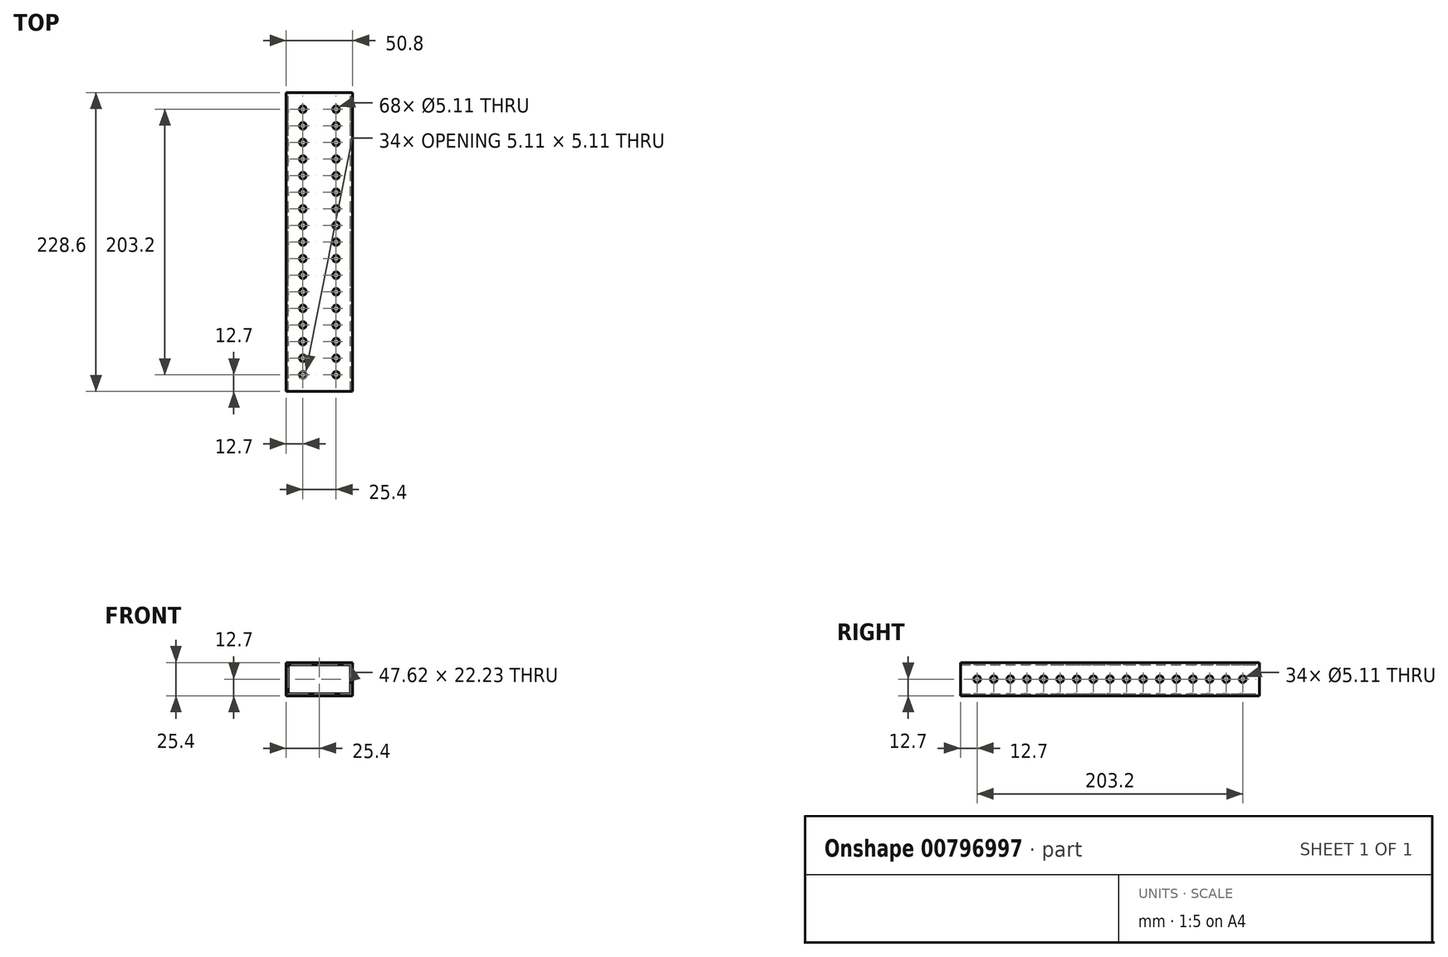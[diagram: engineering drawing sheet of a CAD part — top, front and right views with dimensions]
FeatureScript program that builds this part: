
annotation { "Feature Type Name" : "Feature", "Feature Type Description" : "" }
export const myFeature = defineFeature(function(context is Context, id is Id, definition is map)
    precondition{}
    {
        {
            var Q0;
            Q0=qCreatedBy(makeId("Front.planeOp"),FACE);
            var sketch = newSketch(context, id + "F0", { "sketchPlane" : qUnion([Q0])});
            skLineSegment(sketch, "E0.bottom", {"start": v(-25.4, 12.7) * mm, "end": v(25.4, 12.7) * mm});
            skLineSegment(sketch, "E0.top", {"start": v(-25.4, -12.7) * mm, "end": v(25.4, -12.7) * mm});
            skLineSegment(sketch, "E0.left", {"start": v(-25.4, 12.7) * mm, "end": v(-25.4, -12.7) * mm});
            skLineSegment(sketch, "E0.right", {"start": v(25.4, 12.7) * mm, "end": v(25.4, -12.7) * mm});
            skPoint(sketch, "E0.middle", {"position": v(0, 0) * mm});
            skLineSegment(sketch, "E1.0", {"start": v(-23.81, -11.11) * mm, "end": v(23.81, -11.11) * mm});
            skLineSegment(sketch, "E1.1", {"start": v(-23.81, 11.11) * mm, "end": v(-23.81, -11.11) * mm});
            skLineSegment(sketch, "E1.2", {"start": v(-23.81, 11.11) * mm, "end": v(23.81, 11.11) * mm});
            skLineSegment(sketch, "E1.3", {"start": v(23.81, 11.11) * mm, "end": v(23.81, -11.11) * mm});
            skSolve(sketch);
        }
        {
            var Q0;
            Q0 = qSketchRegion(id + "F0", true);
            extrude(context, id + "F1", {"entities" : qUnion([Q0]), "depth" : 228.6 * mm, "offsetDistance" : 25.4 * mm});
        }
        {
            var Q0;
            Q0=makeQuery(id+"F1.opExtrude","SWEPT_FACE",FACE,{"disambiguationData":[OSD([sQuery(id+"F0.wireOp",EDGE,"E0.left")])]});
            var sketch = newSketch(context, id + "F2", { "sketchPlane" : qUnion([Q0])});
            skCircle(sketch, "E2", {"center": v(12.7, 0) * mm, "radius": 2.55 * mm});
            skCircle(sketch, "E3.1.0.0", {"center": v(25.4, 0) * mm, "radius": 2.55 * mm});
            skCircle(sketch, "E3.2.0.0", {"center": v(38.1, 0) * mm, "radius": 2.55 * mm});
            skCircle(sketch, "E3.3.0.0", {"center": v(50.8, 0) * mm, "radius": 2.55 * mm});
            skCircle(sketch, "E3.4.0.0", {"center": v(63.5, 0) * mm, "radius": 2.55 * mm});
            skCircle(sketch, "E3.5.0.0", {"center": v(76.2, 0) * mm, "radius": 2.55 * mm});
            skCircle(sketch, "E3.6.0.0", {"center": v(88.9, 0) * mm, "radius": 2.55 * mm});
            skCircle(sketch, "E3.7.0.0", {"center": v(101.6, 0) * mm, "radius": 2.55 * mm});
            skCircle(sketch, "E3.8.0.0", {"center": v(114.3, 0) * mm, "radius": 2.55 * mm});
            skCircle(sketch, "E3.9.0.0", {"center": v(127, 0) * mm, "radius": 2.55 * mm});
            skCircle(sketch, "E3.10.0.0", {"center": v(139.7, 0) * mm, "radius": 2.55 * mm});
            skCircle(sketch, "E3.11.0.0", {"center": v(152.4, 0) * mm, "radius": 2.55 * mm});
            skCircle(sketch, "E3.12.0.0", {"center": v(165.1, 0) * mm, "radius": 2.55 * mm});
            skCircle(sketch, "E3.13.0.0", {"center": v(177.8, 0) * mm, "radius": 2.55 * mm});
            skCircle(sketch, "E3.14.0.0", {"center": v(190.5, 0) * mm, "radius": 2.55 * mm});
            skCircle(sketch, "E3.15.0.0", {"center": v(203.2, 0) * mm, "radius": 2.55 * mm});
            skCircle(sketch, "E3.16.0.0", {"center": v(215.9, 0) * mm, "radius": 2.55 * mm});
            skLineSegment(sketch, "E3.direction1", {"start": v(12.7, 0) * mm, "end": v(25.4, 0) * mm, "construction": true});
            skSolve(sketch);
        }
        {
            var Q0;
            Q0=makeQuery(id+"F2.imprint","IMPRINT",FACE,{"disambiguationData":[TD([[makeQuery(id+"F2.imprint","IMPRINT",EDGE,{"derivedFrom":sQuery(id+"F2.wireOp",EDGE,"E2")}),1.0]])]});
            var Q1;
            Q1=makeQuery(id+"F2.imprint","IMPRINT",FACE,{"disambiguationData":[TD([[makeQuery(id+"F2.imprint","IMPRINT",EDGE,{"derivedFrom":sQuery(id+"F2.wireOp",EDGE,"E3.1.0.0")}),1.0]])]});
            var Q2;
            Q2=makeQuery(id+"F2.imprint","IMPRINT",FACE,{"disambiguationData":[TD([[makeQuery(id+"F2.imprint","IMPRINT",EDGE,{"derivedFrom":sQuery(id+"F2.wireOp",EDGE,"E3.2.0.0")}),1.0]])]});
            var Q3;
            Q3=makeQuery(id+"F2.imprint","IMPRINT",FACE,{"disambiguationData":[TD([[makeQuery(id+"F2.imprint","IMPRINT",EDGE,{"derivedFrom":sQuery(id+"F2.wireOp",EDGE,"E3.3.0.0")}),1.0]])]});
            var Q4;
            Q4=makeQuery(id+"F2.imprint","IMPRINT",FACE,{"disambiguationData":[TD([[makeQuery(id+"F2.imprint","IMPRINT",EDGE,{"derivedFrom":sQuery(id+"F2.wireOp",EDGE,"E3.4.0.0")}),1.0]])]});
            var Q5;
            Q5=makeQuery(id+"F2.imprint","IMPRINT",FACE,{"disambiguationData":[TD([[makeQuery(id+"F2.imprint","IMPRINT",EDGE,{"derivedFrom":sQuery(id+"F2.wireOp",EDGE,"E3.6.0.0")}),1.0]])]});
            var Q6;
            Q6=makeQuery(id+"F2.imprint","IMPRINT",FACE,{"disambiguationData":[TD([[makeQuery(id+"F2.imprint","IMPRINT",EDGE,{"derivedFrom":sQuery(id+"F2.wireOp",EDGE,"E3.7.0.0")}),1.0]])]});
            var Q7;
            Q7=makeQuery(id+"F2.imprint","IMPRINT",FACE,{"disambiguationData":[TD([[makeQuery(id+"F2.imprint","IMPRINT",EDGE,{"derivedFrom":sQuery(id+"F2.wireOp",EDGE,"E3.5.0.0")}),1.0]])]});
            var Q8;
            Q8=makeQuery(id+"F2.imprint","IMPRINT",FACE,{"disambiguationData":[TD([[makeQuery(id+"F2.imprint","IMPRINT",EDGE,{"derivedFrom":sQuery(id+"F2.wireOp",EDGE,"E3.8.0.0")}),1.0]])]});
            var Q9;
            Q9=makeQuery(id+"F2.imprint","IMPRINT",FACE,{"disambiguationData":[TD([[makeQuery(id+"F2.imprint","IMPRINT",EDGE,{"derivedFrom":sQuery(id+"F2.wireOp",EDGE,"E3.9.0.0")}),1.0]])]});
            var Q10;
            Q10=makeQuery(id+"F2.imprint","IMPRINT",FACE,{"disambiguationData":[TD([[makeQuery(id+"F2.imprint","IMPRINT",EDGE,{"derivedFrom":sQuery(id+"F2.wireOp",EDGE,"E3.10.0.0")}),1.0]])]});
            var Q11;
            Q11=makeQuery(id+"F2.imprint","IMPRINT",FACE,{"disambiguationData":[TD([[makeQuery(id+"F2.imprint","IMPRINT",EDGE,{"derivedFrom":sQuery(id+"F2.wireOp",EDGE,"E3.11.0.0")}),1.0]])]});
            var Q12;
            Q12=makeQuery(id+"F2.imprint","IMPRINT",FACE,{"disambiguationData":[TD([[makeQuery(id+"F2.imprint","IMPRINT",EDGE,{"derivedFrom":sQuery(id+"F2.wireOp",EDGE,"E3.12.0.0")}),1.0]])]});
            var Q13;
            Q13=makeQuery(id+"F2.imprint","IMPRINT",FACE,{"disambiguationData":[TD([[makeQuery(id+"F2.imprint","IMPRINT",EDGE,{"derivedFrom":sQuery(id+"F2.wireOp",EDGE,"E3.13.0.0")}),1.0]])]});
            var Q14;
            Q14=makeQuery(id+"F2.imprint","IMPRINT",FACE,{"disambiguationData":[TD([[makeQuery(id+"F2.imprint","IMPRINT",EDGE,{"derivedFrom":sQuery(id+"F2.wireOp",EDGE,"E3.14.0.0")}),1.0]])]});
            var Q15;
            Q15=makeQuery(id+"F2.imprint","IMPRINT",FACE,{"disambiguationData":[TD([[makeQuery(id+"F2.imprint","IMPRINT",EDGE,{"derivedFrom":sQuery(id+"F2.wireOp",EDGE,"E3.15.0.0")}),1.0]])]});
            var Q16;
            Q16=makeQuery(id+"F2.imprint","IMPRINT",FACE,{"disambiguationData":[TD([[makeQuery(id+"F2.imprint","IMPRINT",EDGE,{"derivedFrom":sQuery(id+"F2.wireOp",EDGE,"E3.16.0.0")}),1.0]])]});
            var Q17;
            Q17=makeQuery(id+"F2.imprint","IMPRINT",FACE,{"disambiguationData":[TD([[makeQuery(id+"F2.imprint","IMPRINT",EDGE,{"derivedFrom":sQuery(id+"F2.wireOp",EDGE,"E3.17.0.0")}),1.0]])]});
            var Q18;
            Q18=makeQuery(id+"F2.imprint","IMPRINT",FACE,{"disambiguationData":[TD([[makeQuery(id+"F2.imprint","IMPRINT",EDGE,{"derivedFrom":sQuery(id+"F2.wireOp",EDGE,"E3.18.0.0")}),1.0]])]});
            extrude(context, id + "F3", {"entities" : qUnion([Q0, Q1, Q2, Q3, Q4, Q5, Q6, Q7, Q8, Q9, Q10, Q11, Q12, Q13, Q14, Q15, Q16, Q17, Q18]), "operationType" : NewBodyOperationType.REMOVE, "oppositeDirection" : true, "depth" : 279.4 * mm, "offsetDistance" : 25.4 * mm});
        }
        {
            var Q0;
            Q0=makeQuery(id+"F1.opExtrude","SWEPT_FACE",FACE,{"disambiguationData":[OSD([sQuery(id+"F0.wireOp",EDGE,"E0.top")])]});
            var sketch = newSketch(context, id + "F4", { "sketchPlane" : qUnion([Q0])});
            skCircle(sketch, "E4", {"center": v(-12.7, 215.9) * mm, "radius": 2.55 * mm});
            skCircle(sketch, "E5.0.1.0", {"center": v(-12.7, 203.2) * mm, "radius": 2.55 * mm});
            skCircle(sketch, "E5.0.2.0", {"center": v(-12.7, 190.5) * mm, "radius": 2.55 * mm});
            skCircle(sketch, "E5.0.3.0", {"center": v(-12.7, 177.8) * mm, "radius": 2.55 * mm});
            skCircle(sketch, "E5.0.4.0", {"center": v(-12.7, 165.1) * mm, "radius": 2.55 * mm});
            skCircle(sketch, "E5.0.5.0", {"center": v(-12.7, 152.4) * mm, "radius": 2.55 * mm});
            skCircle(sketch, "E5.0.6.0", {"center": v(-12.7, 139.7) * mm, "radius": 2.55 * mm});
            skCircle(sketch, "E5.0.7.0", {"center": v(-12.7, 127) * mm, "radius": 2.55 * mm});
            skCircle(sketch, "E5.0.8.0", {"center": v(-12.7, 114.3) * mm, "radius": 2.55 * mm});
            skCircle(sketch, "E5.0.9.0", {"center": v(-12.7, 101.6) * mm, "radius": 2.55 * mm});
            skCircle(sketch, "E5.0.10.0", {"center": v(-12.7, 88.9) * mm, "radius": 2.55 * mm});
            skCircle(sketch, "E5.0.11.0", {"center": v(-12.7, 76.2) * mm, "radius": 2.55 * mm});
            skCircle(sketch, "E5.0.12.0", {"center": v(-12.7, 63.5) * mm, "radius": 2.55 * mm});
            skCircle(sketch, "E5.0.13.0", {"center": v(-12.7, 50.8) * mm, "radius": 2.55 * mm});
            skCircle(sketch, "E5.0.14.0", {"center": v(-12.7, 38.1) * mm, "radius": 2.55 * mm});
            skCircle(sketch, "E5.0.15.0", {"center": v(-12.7, 25.4) * mm, "radius": 2.55 * mm});
            skCircle(sketch, "E5.0.16.0", {"center": v(-12.7, 12.7) * mm, "radius": 2.55 * mm});
            skCircle(sketch, "E5.1.0.0", {"center": v(12.7, 215.9) * mm, "radius": 2.55 * mm});
            skCircle(sketch, "E5.1.1.0", {"center": v(12.7, 203.2) * mm, "radius": 2.55 * mm});
            skCircle(sketch, "E5.1.2.0", {"center": v(12.7, 190.5) * mm, "radius": 2.55 * mm});
            skCircle(sketch, "E5.1.3.0", {"center": v(12.7, 177.8) * mm, "radius": 2.55 * mm});
            skCircle(sketch, "E5.1.4.0", {"center": v(12.7, 165.1) * mm, "radius": 2.55 * mm});
            skCircle(sketch, "E5.1.5.0", {"center": v(12.7, 152.4) * mm, "radius": 2.55 * mm});
            skCircle(sketch, "E5.1.6.0", {"center": v(12.7, 139.7) * mm, "radius": 2.55 * mm});
            skCircle(sketch, "E5.1.7.0", {"center": v(12.7, 127) * mm, "radius": 2.55 * mm});
            skCircle(sketch, "E5.1.8.0", {"center": v(12.7, 114.3) * mm, "radius": 2.55 * mm});
            skCircle(sketch, "E5.1.9.0", {"center": v(12.7, 101.6) * mm, "radius": 2.55 * mm});
            skCircle(sketch, "E5.1.10.0", {"center": v(12.7, 88.9) * mm, "radius": 2.55 * mm});
            skCircle(sketch, "E5.1.11.0", {"center": v(12.7, 76.2) * mm, "radius": 2.55 * mm});
            skCircle(sketch, "E5.1.12.0", {"center": v(12.7, 63.5) * mm, "radius": 2.55 * mm});
            skCircle(sketch, "E5.1.13.0", {"center": v(12.7, 50.8) * mm, "radius": 2.55 * mm});
            skCircle(sketch, "E5.1.14.0", {"center": v(12.7, 38.1) * mm, "radius": 2.55 * mm});
            skCircle(sketch, "E5.1.15.0", {"center": v(12.7, 25.4) * mm, "radius": 2.55 * mm});
            skCircle(sketch, "E5.1.16.0", {"center": v(12.7, 12.7) * mm, "radius": 2.55 * mm});
            skLineSegment(sketch, "E5.direction1", {"start": v(-12.7, 215.9) * mm, "end": v(12.7, 215.9) * mm, "construction": true});
            skLineSegment(sketch, "E5.direction2", {"start": v(-12.7, 215.9) * mm, "end": v(-12.7, 203.2) * mm, "construction": true});
            skLineSegment(sketch, "E6.bottom", {"start": v(-25.4, 228.6) * mm, "end": v(25.4, 228.6) * mm});
            skLineSegment(sketch, "E6.top", {"start": v(-25.4, 0) * mm, "end": v(25.4, 0) * mm});
            skLineSegment(sketch, "E6.left", {"start": v(-25.4, 228.6) * mm, "end": v(-25.4, 0) * mm});
            skLineSegment(sketch, "E6.right", {"start": v(25.4, 228.6) * mm, "end": v(25.4, 0) * mm});
            skSolve(sketch);
        }
        {
            var Q0;
            Q0=makeQuery(id+"F4.imprint","IMPRINT",FACE,{"disambiguationData":[TD([[makeQuery(id+"F4.imprint","IMPRINT",EDGE,{"derivedFrom":sQuery(id+"F4.wireOp",EDGE,"E5.1.15.0")}),1.0]])]});
            var Q1;
            Q1=makeQuery(id+"F4.imprint","IMPRINT",FACE,{"disambiguationData":[TD([[makeQuery(id+"F4.imprint","IMPRINT",EDGE,{"derivedFrom":sQuery(id+"F4.wireOp",EDGE,"E5.0.15.0")}),1.0]])]});
            var Q2;
            Q2=makeQuery(id+"F4.imprint","IMPRINT",FACE,{"disambiguationData":[TD([[makeQuery(id+"F4.imprint","IMPRINT",EDGE,{"derivedFrom":sQuery(id+"F4.wireOp",EDGE,"E5.0.7.0")}),1.0]])]});
            var Q3;
            Q3=makeQuery(id+"F4.imprint","IMPRINT",FACE,{"disambiguationData":[TD([[makeQuery(id+"F4.imprint","IMPRINT",EDGE,{"derivedFrom":sQuery(id+"F4.wireOp",EDGE,"E5.0.9.0")}),1.0]])]});
            var Q4;
            Q4=makeQuery(id+"F4.imprint","IMPRINT",FACE,{"disambiguationData":[TD([[makeQuery(id+"F4.imprint","IMPRINT",EDGE,{"derivedFrom":sQuery(id+"F4.wireOp",EDGE,"E5.1.17.0")}),1.0]])]});
            var Q5;
            Q5=makeQuery(id+"F4.imprint","IMPRINT",FACE,{"disambiguationData":[TD([[makeQuery(id+"F4.imprint","IMPRINT",EDGE,{"derivedFrom":sQuery(id+"F4.wireOp",EDGE,"E5.1.18.0")}),1.0]])]});
            var Q6;
            Q6=makeQuery(id+"F4.imprint","IMPRINT",FACE,{"disambiguationData":[TD([[makeQuery(id+"F4.imprint","IMPRINT",EDGE,{"derivedFrom":sQuery(id+"F4.wireOp",EDGE,"E5.1.5.0")}),1.0]])]});
            var Q7;
            Q7=makeQuery(id+"F4.imprint","IMPRINT",FACE,{"disambiguationData":[TD([[makeQuery(id+"F4.imprint","IMPRINT",EDGE,{"derivedFrom":sQuery(id+"F4.wireOp",EDGE,"E5.0.3.0")}),1.0]])]});
            var Q8;
            Q8=makeQuery(id+"F4.imprint","IMPRINT",FACE,{"disambiguationData":[TD([[makeQuery(id+"F4.imprint","IMPRINT",EDGE,{"derivedFrom":sQuery(id+"F4.wireOp",EDGE,"E5.1.12.0")}),1.0]])]});
            var Q9;
            Q9=makeQuery(id+"F4.imprint","IMPRINT",FACE,{"disambiguationData":[TD([[makeQuery(id+"F4.imprint","IMPRINT",EDGE,{"derivedFrom":sQuery(id+"F4.wireOp",EDGE,"E5.1.2.0")}),1.0]])]});
            var Q10;
            Q10=makeQuery(id+"F4.imprint","IMPRINT",FACE,{"disambiguationData":[TD([[makeQuery(id+"F4.imprint","IMPRINT",EDGE,{"derivedFrom":sQuery(id+"F4.wireOp",EDGE,"E5.1.9.0")}),1.0]])]});
            var Q11;
            Q11=makeQuery(id+"F4.imprint","IMPRINT",FACE,{"disambiguationData":[TD([[makeQuery(id+"F4.imprint","IMPRINT",EDGE,{"derivedFrom":sQuery(id+"F4.wireOp",EDGE,"E5.0.11.0")}),1.0]])]});
            var Q12;
            Q12=makeQuery(id+"F4.imprint","IMPRINT",FACE,{"disambiguationData":[TD([[makeQuery(id+"F4.imprint","IMPRINT",EDGE,{"derivedFrom":sQuery(id+"F4.wireOp",EDGE,"E5.0.6.0")}),1.0]])]});
            var Q13;
            Q13=makeQuery(id+"F4.imprint","IMPRINT",FACE,{"disambiguationData":[TD([[makeQuery(id+"F4.imprint","IMPRINT",EDGE,{"derivedFrom":sQuery(id+"F4.wireOp",EDGE,"E5.1.16.0")}),1.0]])]});
            var Q14;
            Q14=makeQuery(id+"F4.imprint","IMPRINT",FACE,{"disambiguationData":[TD([[makeQuery(id+"F4.imprint","IMPRINT",EDGE,{"derivedFrom":sQuery(id+"F4.wireOp",EDGE,"E5.1.11.0")}),1.0]])]});
            var Q15;
            Q15=makeQuery(id+"F4.imprint","IMPRINT",FACE,{"disambiguationData":[TD([[makeQuery(id+"F4.imprint","IMPRINT",EDGE,{"derivedFrom":sQuery(id+"F4.wireOp",EDGE,"E5.1.13.0")}),1.0]])]});
            var Q16;
            Q16=makeQuery(id+"F4.imprint","IMPRINT",FACE,{"disambiguationData":[TD([[makeQuery(id+"F4.imprint","IMPRINT",EDGE,{"derivedFrom":sQuery(id+"F4.wireOp",EDGE,"E5.1.10.0")}),1.0]])]});
            var Q17;
            Q17=makeQuery(id+"F4.imprint","IMPRINT",FACE,{"disambiguationData":[TD([[makeQuery(id+"F4.imprint","IMPRINT",EDGE,{"derivedFrom":sQuery(id+"F4.wireOp",EDGE,"E5.1.6.0")}),1.0]])]});
            var Q18;
            Q18=makeQuery(id+"F4.imprint","IMPRINT",FACE,{"disambiguationData":[TD([[makeQuery(id+"F4.imprint","IMPRINT",EDGE,{"derivedFrom":sQuery(id+"F4.wireOp",EDGE,"E5.1.3.0")}),1.0]])]});
            var Q19;
            Q19=makeQuery(id+"F4.imprint","IMPRINT",FACE,{"disambiguationData":[TD([[makeQuery(id+"F4.imprint","IMPRINT",EDGE,{"derivedFrom":sQuery(id+"F4.wireOp",EDGE,"E5.0.18.0")}),1.0]])]});
            var Q20;
            Q20=makeQuery(id+"F4.imprint","IMPRINT",FACE,{"disambiguationData":[TD([[makeQuery(id+"F4.imprint","IMPRINT",EDGE,{"derivedFrom":sQuery(id+"F4.wireOp",EDGE,"E5.1.4.0")}),1.0]])]});
            var Q21;
            Q21=makeQuery(id+"F4.imprint","IMPRINT",FACE,{"disambiguationData":[TD([[makeQuery(id+"F4.imprint","IMPRINT",EDGE,{"derivedFrom":sQuery(id+"F4.wireOp",EDGE,"E5.0.2.0")}),1.0]])]});
            var Q22;
            Q22=makeQuery(id+"F4.imprint","IMPRINT",FACE,{"disambiguationData":[TD([[makeQuery(id+"F4.imprint","IMPRINT",EDGE,{"derivedFrom":sQuery(id+"F4.wireOp",EDGE,"E5.1.14.0")}),1.0]])]});
            var Q23;
            Q23=makeQuery(id+"F4.imprint","IMPRINT",FACE,{"disambiguationData":[TD([[makeQuery(id+"F4.imprint","IMPRINT",EDGE,{"derivedFrom":sQuery(id+"F4.wireOp",EDGE,"E5.0.14.0")}),1.0]])]});
            var Q24;
            Q24=makeQuery(id+"F4.imprint","IMPRINT",FACE,{"disambiguationData":[TD([[makeQuery(id+"F4.imprint","IMPRINT",EDGE,{"derivedFrom":sQuery(id+"F4.wireOp",EDGE,"E5.0.17.0")}),1.0]])]});
            var Q25;
            Q25=makeQuery(id+"F4.imprint","IMPRINT",FACE,{"disambiguationData":[TD([[makeQuery(id+"F4.imprint","IMPRINT",EDGE,{"derivedFrom":sQuery(id+"F4.wireOp",EDGE,"E5.1.1.0")}),1.0]])]});
            var Q26;
            Q26=makeQuery(id+"F4.imprint","IMPRINT",FACE,{"disambiguationData":[TD([[makeQuery(id+"F4.imprint","IMPRINT",EDGE,{"derivedFrom":sQuery(id+"F4.wireOp",EDGE,"E5.0.12.0")}),1.0]])]});
            var Q27;
            Q27=makeQuery(id+"F4.imprint","IMPRINT",FACE,{"disambiguationData":[TD([[makeQuery(id+"F4.imprint","IMPRINT",EDGE,{"derivedFrom":sQuery(id+"F4.wireOp",EDGE,"E5.1.7.0")}),1.0]])]});
            var Q28;
            Q28=makeQuery(id+"F4.imprint","IMPRINT",FACE,{"disambiguationData":[TD([[makeQuery(id+"F4.imprint","IMPRINT",EDGE,{"derivedFrom":sQuery(id+"F4.wireOp",EDGE,"E5.0.4.0")}),1.0]])]});
            var Q29;
            Q29=makeQuery(id+"F4.imprint","IMPRINT",FACE,{"disambiguationData":[TD([[makeQuery(id+"F4.imprint","IMPRINT",EDGE,{"derivedFrom":sQuery(id+"F4.wireOp",EDGE,"E5.0.10.0")}),1.0]])]});
            var Q30;
            Q30=makeQuery(id+"F4.imprint","IMPRINT",FACE,{"disambiguationData":[TD([[makeQuery(id+"F4.imprint","IMPRINT",EDGE,{"derivedFrom":sQuery(id+"F4.wireOp",EDGE,"E5.1.8.0")}),1.0]])]});
            var Q31;
            Q31=makeQuery(id+"F4.imprint","IMPRINT",FACE,{"disambiguationData":[TD([[makeQuery(id+"F4.imprint","IMPRINT",EDGE,{"derivedFrom":sQuery(id+"F4.wireOp",EDGE,"E5.0.8.0")}),1.0]])]});
            var Q32;
            Q32=makeQuery(id+"F4.imprint","IMPRINT",FACE,{"disambiguationData":[TD([[makeQuery(id+"F4.imprint","IMPRINT",EDGE,{"derivedFrom":sQuery(id+"F4.wireOp",EDGE,"E5.0.5.0")}),1.0]])]});
            var Q33;
            Q33=makeQuery(id+"F4.imprint","IMPRINT",FACE,{"disambiguationData":[TD([[makeQuery(id+"F4.imprint","IMPRINT",EDGE,{"derivedFrom":sQuery(id+"F4.wireOp",EDGE,"E5.0.1.0")}),1.0]])]});
            var Q34;
            Q34=makeQuery(id+"F4.imprint","IMPRINT",FACE,{"disambiguationData":[TD([[makeQuery(id+"F4.imprint","IMPRINT",EDGE,{"derivedFrom":sQuery(id+"F4.wireOp",EDGE,"E5.0.16.0")}),1.0]])]});
            var Q35;
            Q35=makeQuery(id+"F4.imprint","IMPRINT",FACE,{"disambiguationData":[TD([[makeQuery(id+"F4.imprint","IMPRINT",EDGE,{"derivedFrom":sQuery(id+"F4.wireOp",EDGE,"E5.0.13.0")}),1.0]])]});
            var Q36;
            Q36=makeQuery(id+"F4.imprint","IMPRINT",FACE,{"disambiguationData":[TD([[makeQuery(id+"F4.imprint","IMPRINT",EDGE,{"derivedFrom":sQuery(id+"F4.wireOp",EDGE,"E5.1.0.0")}),1.0]])]});
            var Q37;
            Q37=makeQuery(id+"F4.imprint","IMPRINT",FACE,{"disambiguationData":[TD([[makeQuery(id+"F4.imprint","IMPRINT",EDGE,{"derivedFrom":sQuery(id+"F4.wireOp",EDGE,"E4")}),1.0]])]});
            extrude(context, id + "F5", {"entities" : qUnion([Q0, Q1, Q2, Q3, Q4, Q5, Q6, Q7, Q8, Q9, Q10, Q11, Q12, Q13, Q14, Q15, Q16, Q17, Q18, Q19, Q20, Q21, Q22, Q23, Q24, Q25, Q26, Q27, Q28, Q29, Q30, Q31, Q32, Q33, Q34, Q35, Q36, Q37]), "operationType" : NewBodyOperationType.REMOVE, "oppositeDirection" : true, "depth" : 25.4 * mm, "offsetDistance" : 25.4 * mm});
        }
    });
